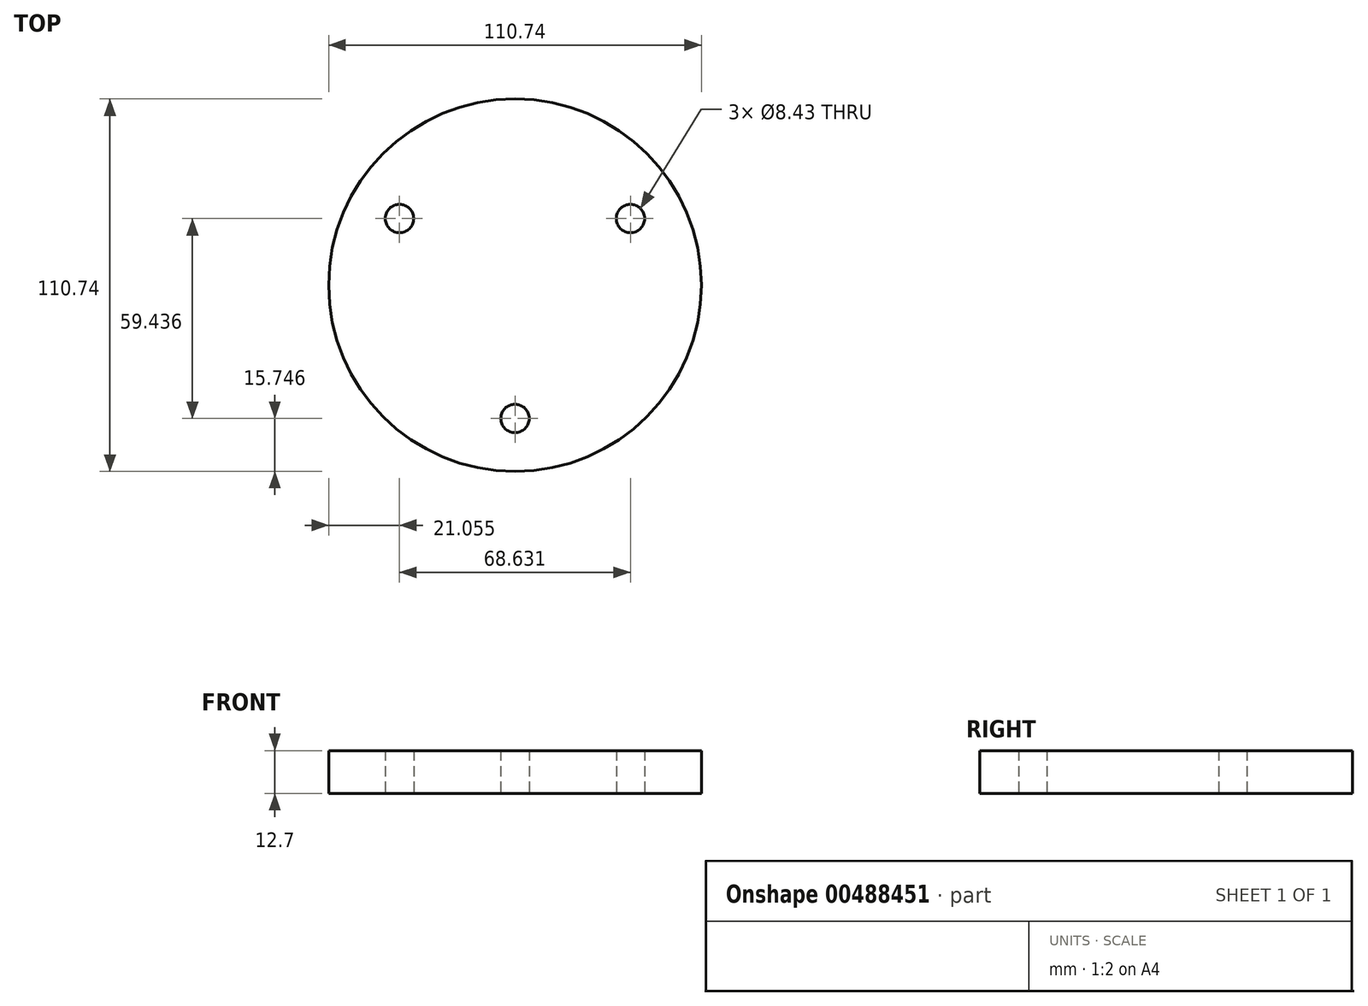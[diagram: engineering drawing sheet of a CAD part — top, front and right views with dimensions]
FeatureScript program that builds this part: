
annotation { "Feature Type Name" : "Feature", "Feature Type Description" : "" }
export const myFeature = defineFeature(function(context is Context, id is Id, definition is map)
    precondition{}
    {
        {
            var Q0;
            Q0=qCreatedBy(makeId("Top.planeOp"),FACE);
            var sketch = newSketch(context, id + "F0", { "sketchPlane" : qUnion([Q0])});
            skCircle(sketch, "E0", {"center": v(0, 0) * mm, "radius": 55.37 * mm});
            skCircle(sketch, "E1", {"center": v(0, 0) * mm, "radius": 39.62 * mm});
            skCircle(sketch, "E2", {"center": v(-34.32, 19.81) * mm, "radius": 4.22 * mm});
            skCircle(sketch, "E3", {"center": v(34.32, 19.81) * mm, "radius": 4.22 * mm});
            skCircle(sketch, "E4", {"center": v(0, -39.62) * mm, "radius": 4.22 * mm});
            skLineSegment(sketch, "E5", {"start": v(-34.32, 19.81) * mm, "end": v(0, 0) * mm});
            skLineSegment(sketch, "E6", {"start": v(34.32, 19.81) * mm, "end": v(0, 0) * mm});
            skLineSegment(sketch, "E7", {"start": v(0, -39.62) * mm, "end": v(0, 0) * mm});
            skSolve(sketch);
        }
        {
            var Q0;
            Q0=makeQuery(id+"F0.imprint","IMPRINT",FACE,{"disambiguationData":[TD([[makeQuery(id+"F0.imprint","IMPRINT",EDGE,{"derivedFrom":sQuery(id+"F0.wireOp",EDGE,"E0")}),1.0]])]});
            var Q1;
            {var subQ5=sQuery(id+"F0.wireOp",EDGE,"E1");var subQ7=sQuery(id+"F0.wireOp",EDGE,"E3");var subQ8=makeQuery(id+"F0.imprint","INTERSECT",VERTEX,{"disambiguationData":[OD(1.0)],"derivedFrom":[subQ5,subQ7]});Q1=makeQuery(id+"F0.imprint","IMPRINT",FACE,{"disambiguationData":[TD([[makeQuery(id+"F0.imprint","IMPRINT",EDGE,{"disambiguationData":[TD([[subQ8,-1.0]])],"derivedFrom":subQ5}),1.0]])]});}
            var Q2;
            {var subQ3=sQuery(id+"F0.wireOp",EDGE,"E2");var subQ6=sQuery(id+"F0.wireOp",EDGE,"E1");var subQ9=makeQuery(id+"F0.imprint","INTERSECT",VERTEX,{"disambiguationData":[OD(1.0)],"derivedFrom":[subQ6,subQ3]});Q2=makeQuery(id+"F0.imprint","IMPRINT",FACE,{"disambiguationData":[TD([[makeQuery(id+"F0.imprint","IMPRINT",EDGE,{"disambiguationData":[TD([[subQ9,-1.0]])],"derivedFrom":subQ6}),1.0]])]});}
            var Q3;
            {var subQ3=sQuery(id+"F0.wireOp",EDGE,"E3");var subQ6=sQuery(id+"F0.wireOp",EDGE,"E1");var subQ9=makeQuery(id+"F0.imprint","INTERSECT",VERTEX,{"disambiguationData":[OD(0.0)],"derivedFrom":[subQ6,subQ3]});Q3=makeQuery(id+"F0.imprint","IMPRINT",FACE,{"disambiguationData":[TD([[makeQuery(id+"F0.imprint","IMPRINT",EDGE,{"disambiguationData":[TD([[subQ9,1.0]])],"derivedFrom":subQ6}),1.0]])]});}
            extrude(context, id + "F1", {"entities" : qUnion([Q0, Q1, Q2, Q3]), "depth" : 12.7 * mm});
        }
    });
